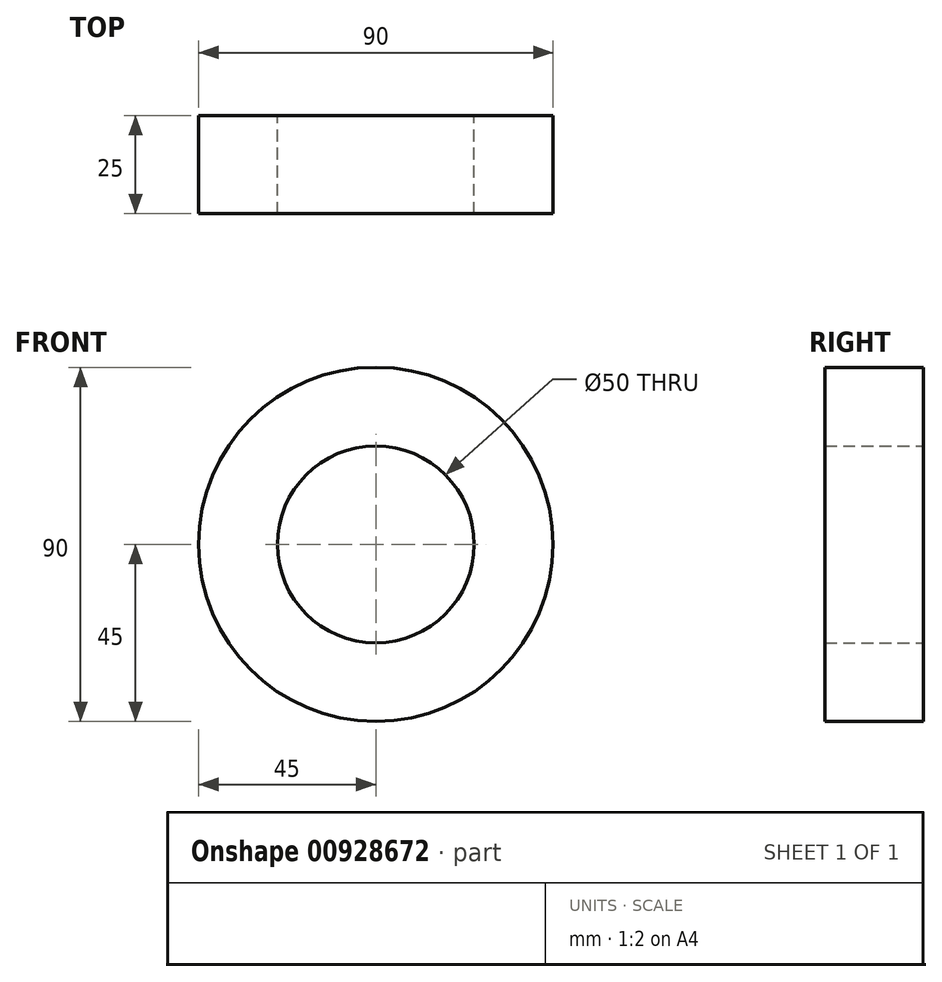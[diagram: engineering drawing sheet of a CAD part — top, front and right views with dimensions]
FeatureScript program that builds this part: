
annotation { "Feature Type Name" : "Feature", "Feature Type Description" : "" }
export const myFeature = defineFeature(function(context is Context, id is Id, definition is map)
    precondition{}
    {
        {
            var Q0;
            Q0=qCreatedBy(makeId("Front.planeOp"),FACE);
            var sketch = newSketch(context, id + "F0", { "sketchPlane" : qUnion([Q0])});
            skCircle(sketch, "E0", {"center": v(0, 0) * mm, "radius": 45 * mm});
            skCircle(sketch, "E1", {"center": v(0, 0) * mm, "radius": 25 * mm});
            skLineSegment(sketch, "E2", {"start": v(0, 45) * mm, "end": v(0, -45) * mm});
            skLineSegment(sketch, "E3", {"start": v(0, -45) * mm, "end": v(-45, 0) * mm});
            skLineSegment(sketch, "E4", {"start": v(-45, 0) * mm, "end": v(0, 45) * mm});
            skLineSegment(sketch, "E5", {"start": v(0, 45) * mm, "end": v(45, 0) * mm});
            skLineSegment(sketch, "E6", {"start": v(45, 0) * mm, "end": v(0, -45) * mm});
            skSolve(sketch);
        }
        {
            var Q0;
            Q0 = qSketchRegion(id + "F0", true);
            extrude(context, id + "F1", {"entities" : qUnion([Q0]), "depth" : 25 * mm, "offsetDistance" : 25 * mm});
        }
    });
